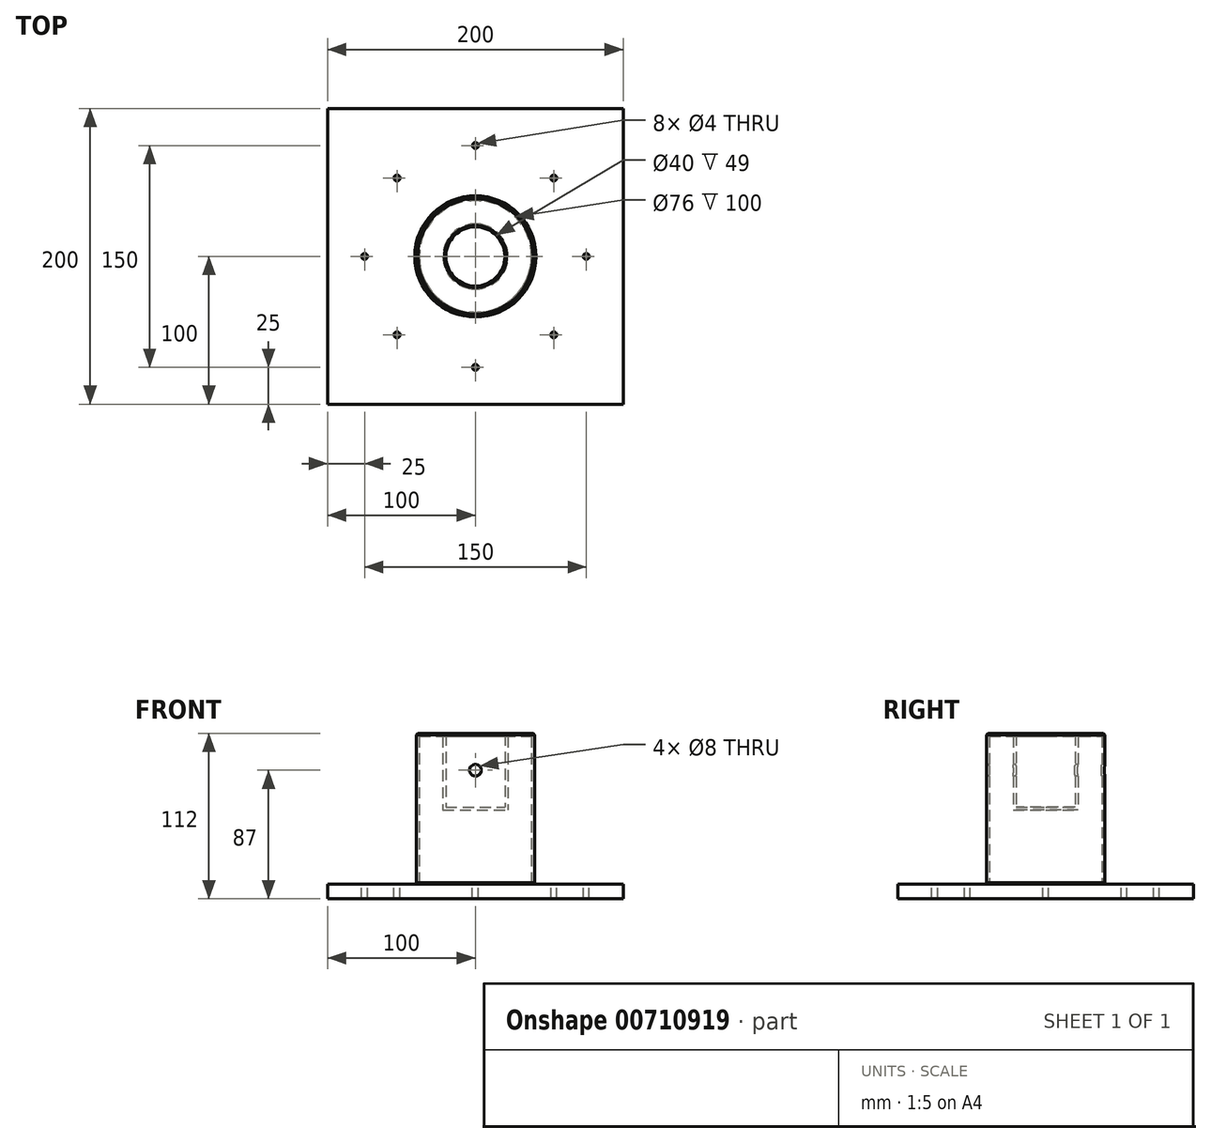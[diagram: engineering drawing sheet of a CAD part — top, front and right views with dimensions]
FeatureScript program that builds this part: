
annotation { "Feature Type Name" : "Feature", "Feature Type Description" : "" }
export const myFeature = defineFeature(function(context is Context, id is Id, definition is map)
    precondition{}
    {
        {
            var Q0;
            Q0=qCreatedBy(makeId("Top.planeOp"),FACE);
            var sketch = newSketch(context, id + "F0", { "sketchPlane" : qUnion([Q0])});
            skLineSegment(sketch, "E0.bottom", {"start": v(100, 100) * mm, "end": v(-100, 100) * mm});
            skLineSegment(sketch, "E0.top", {"start": v(100, -100) * mm, "end": v(-100, -100) * mm});
            skLineSegment(sketch, "E0.left", {"start": v(100, 100) * mm, "end": v(100, -100) * mm});
            skLineSegment(sketch, "E0.right", {"start": v(-100, 100) * mm, "end": v(-100, -100) * mm});
            skPoint(sketch, "E0.middle", {"position": v(0, 0) * mm});
            skCircle(sketch, "E1", {"center": v(0, 0) * mm, "radius": 75 * mm, "construction": true});
            skLineSegment(sketch, "E2", {"start": v(0, 0) * mm, "end": v(0, 75) * mm, "construction": true});
            skLineSegment(sketch, "E3.1.0", {"start": v(0, 0) * mm, "end": v(-53.03, 53.03) * mm, "construction": true});
            skLineSegment(sketch, "E3.2.0", {"start": v(0, 0) * mm, "end": v(-75, 0) * mm, "construction": true});
            skLineSegment(sketch, "E3.3.0", {"start": v(0, 0) * mm, "end": v(-53.03, -53.03) * mm, "construction": true});
            skLineSegment(sketch, "E3.4.0", {"start": v(0, 0) * mm, "end": v(0, -75) * mm, "construction": true});
            skLineSegment(sketch, "E3.5.0", {"start": v(0, 0) * mm, "end": v(53.03, -53.03) * mm, "construction": true});
            skLineSegment(sketch, "E3.6.0", {"start": v(0, 0) * mm, "end": v(75, 0) * mm, "construction": true});
            skLineSegment(sketch, "E3.7.0", {"start": v(0, 0) * mm, "end": v(53.03, 53.03) * mm, "construction": true});
            skCircle(sketch, "E4", {"center": v(0, 75) * mm, "radius": 2 * mm});
            skCircle(sketch, "E5.1.0", {"center": v(-53.03, 53.03) * mm, "radius": 2 * mm});
            skCircle(sketch, "E5.2.0", {"center": v(-75, 0) * mm, "radius": 2 * mm});
            skCircle(sketch, "E5.3.0", {"center": v(-53.03, -53.03) * mm, "radius": 2 * mm});
            skCircle(sketch, "E5.4.0", {"center": v(0, -75) * mm, "radius": 2 * mm});
            skCircle(sketch, "E5.5.0", {"center": v(53.03, -53.03) * mm, "radius": 2 * mm});
            skCircle(sketch, "E5.6.0", {"center": v(75, 0) * mm, "radius": 2 * mm});
            skCircle(sketch, "E5.7.0", {"center": v(53.03, 53.03) * mm, "radius": 2 * mm});
            skSolve(sketch);
        }
        {
            var Q0;
            Q0=makeQuery(id+"F0.imprint","IMPRINT",FACE,{"disambiguationData":[TD([[makeQuery(id+"F0.imprint","IMPRINT",EDGE,{"derivedFrom":sQuery(id+"F0.wireOp",EDGE,"E0.bottom")}),1.0]])]});
            extrude(context, id + "F1", {"entities" : qUnion([Q0]), "oppositeDirection" : true, "depth" : 10 * mm, "offsetDistance" : 25 * mm});
        }
        {
            var Q0;
            Q0=makeQuery(id+"F1.opExtrude","CAP_FACE",FACE,{"disambiguationData":[OSD([sQuery(id+"F0.wireOp",EDGE,"E0.bottom"),sQuery(id+"F0.wireOp",EDGE,"E0.top"),sQuery(id+"F0.wireOp",EDGE,"E0.left"),sQuery(id+"F0.wireOp",EDGE,"E0.right"),sQuery(id+"F0.wireOp",EDGE,"UspNWtAe-SIwK-JmW5-1ujy-vKTlffoFaMBX"),sQuery(id+"F0.wireOp",EDGE,"4a3c6f45-c082-4233-93ed-6daf78118f370.MirrorC"),sQuery(id+"F0.wireOp",EDGE,"ecb49b55-6abf-4db5-afd3-f874b894327a0.MirrorC"),sQuery(id+"F0.wireOp",EDGE,"d2dec525-fc7c-4e63-9322-aa50b5d55a1c0.MirrorC")])],"isStart":true});
            var sketch = newSketch(context, id + "F2", { "sketchPlane" : qUnion([Q0])});
            skCircle(sketch, "E6", {"center": v(0, 0) * mm, "radius": 40 * mm});
            skCircle(sketch, "E7.0", {"center": v(0, 0) * mm, "radius": 38 * mm});
            skSolve(sketch);
        }
        {
            var Q0;
            Q0=makeQuery(id+"F2.imprint","IMPRINT",FACE,{"disambiguationData":[TD([[makeQuery(id+"F2.imprint","IMPRINT",EDGE,{"derivedFrom":sQuery(id+"F2.wireOp",EDGE,"E6")}),1.0]])]});
            extrude(context, id + "F3", {"entities" : qUnion([Q0]), "operationType" : NewBodyOperationType.ADD, "depth" : 100 * mm, "offsetDistance" : 25 * mm});
        }
        {
            var Q0;
            Q0=makeQuery(id+"F3.opExtrude","CAP_FACE",FACE,{"disambiguationData":[OSD([sQuery(id+"F2.wireOp",EDGE,"E6"),sQuery(id+"F2.wireOp",EDGE,"E7.0")])],"isStart":false});
            var sketch = newSketch(context, id + "F4", { "sketchPlane" : qUnion([Q0])});
            skCircle(sketch, "E8", {"center": v(0, 0) * mm, "radius": 39.92 * mm});
            skSolve(sketch);
        }
        {
            var Q0;
            Q0=qCreatedBy(makeId("Front.planeOp"),FACE);
            var sketch = newSketch(context, id + "F5", { "sketchPlane" : qUnion([Q0])});
            skLineSegment(sketch, "E9", {"start": v(0, 50) * mm, "end": v(22, 50) * mm});
            skLineSegment(sketch, "E10", {"start": v(22, 50) * mm, "end": v(22, 100) * mm});
            skLineSegment(sketch, "E11", {"start": v(22, 100) * mm, "end": v(40, 100) * mm});
            skLineSegment(sketch, "E12", {"start": v(40, 100) * mm, "end": v(40, 102) * mm});
            skLineSegment(sketch, "E13", {"start": v(40, 102) * mm, "end": v(20, 102) * mm});
            skLineSegment(sketch, "E14", {"start": v(20, 102) * mm, "end": v(20, 52) * mm});
            skLineSegment(sketch, "E15", {"start": v(20, 52) * mm, "end": v(0, 52) * mm});
            skLineSegment(sketch, "E16", {"start": v(0, 52) * mm, "end": v(0, 50) * mm});
            skLineSegment(sketch, "E17", {"start": v(0, 50) * mm, "end": v(0, 100.3) * mm, "construction": true});
            skSolve(sketch);
        }
        {
            var Q0;
            Q0=makeQuery(id+"F5.imprint","IMPRINT",FACE,{"disambiguationData":[TD([[makeQuery(id+"F5.imprint","IMPRINT",EDGE,{"derivedFrom":sQuery(id+"F5.wireOp",EDGE,"E9")}),1.0]])]});
            var Q1;
            Q1=sQuery(id+"F5.wireOp",EDGE,"E17");
            revolve(context, id + "F6", {"operationType" : NewBodyOperationType.ADD, "entities" : qUnion([Q0]), "axis" : qUnion([Q1]), "revolveType" : RevolveType.FULL});
        }
        {
            var Q0;
            Q0=makeQuery(id+"F6.boolean.opBoolean","MERGE",FACE,{"derivedFrom":[makeQuery(id+"F3.opExtrude","SWEPT_FACE",FACE,{"disambiguationData":[OSD([sQuery(id+"F2.wireOp",EDGE,"E6")])]}),makeQuery(id+"F6.opRevolve","SWEPT_FACE",FACE,{"disambiguationData":[OSD([sQuery(id+"F5.wireOp",EDGE,"E12")])]})]});
            chamfer(context, id + "F7", {"entities" : qUnion([Q0]), "width" : 1 * mm, "tangentPropagation" : true});
        }
        {
            var Q0;
            Q0=makeQuery(id+"F6.opRevolve","SWEPT_EDGE",EDGE,{"disambiguationData":[OSD([sQuery(id+"F5.wireOp",EDGE,"E13"),sQuery(id+"F5.wireOp",EDGE,"E14")])]});
            chamfer(context, id + "F8", {"entities" : qUnion([Q0]), "width" : 1 * mm, "tangentPropagation" : true});
        }
        {
            var Q0;
            Q0=qCreatedBy(makeId("Front.planeOp"),FACE);
            cPlane(context, id + "F9", {"entities" : qUnion([Q0]), "cplaneType" : CPlaneType.OFFSET, "offset" : 40 * mm, "width" : 150 * mm, "height" : 150 * mm});
        }
        {
            var Q0;
            Q0=qCreatedBy(id+"F9.planeOp",FACE);
            var sketch = newSketch(context, id + "F10", { "sketchPlane" : qUnion([Q0])});
            skCircle(sketch, "E18", {"center": v(0, 77) * mm, "radius": 4 * mm});
            skSolve(sketch);
        }
        {
            var Q0;
            Q0=makeQuery(id+"F10.imprint","IMPRINT",FACE,{"disambiguationData":[TD([[makeQuery(id+"F10.imprint","IMPRINT",EDGE,{"derivedFrom":sQuery(id+"F10.wireOp",EDGE,"E18")}),1.0]])]});
            extrude(context, id + "F11", {"entities" : qUnion([Q0]), "operationType" : NewBodyOperationType.REMOVE, "oppositeDirection" : true, "depth" : 80 * mm, "offsetDistance" : 25 * mm});
        }
        {
            var Q0;
            Q0=makeQuery(id+"F0.imprint","IMPRINT",FACE,{"disambiguationData":[TD([[makeQuery(id+"F0.imprint","IMPRINT",EDGE,{"derivedFrom":sQuery(id+"F0.wireOp",EDGE,"E4")}),1.0]])]});
            extrude(context, id + "F12", {"entities" : qUnion([Q0]), "operationType" : NewBodyOperationType.REMOVE, "oppositeDirection" : true, "depth" : 25 * mm, "offsetDistance" : 25 * mm});
        }
    });
